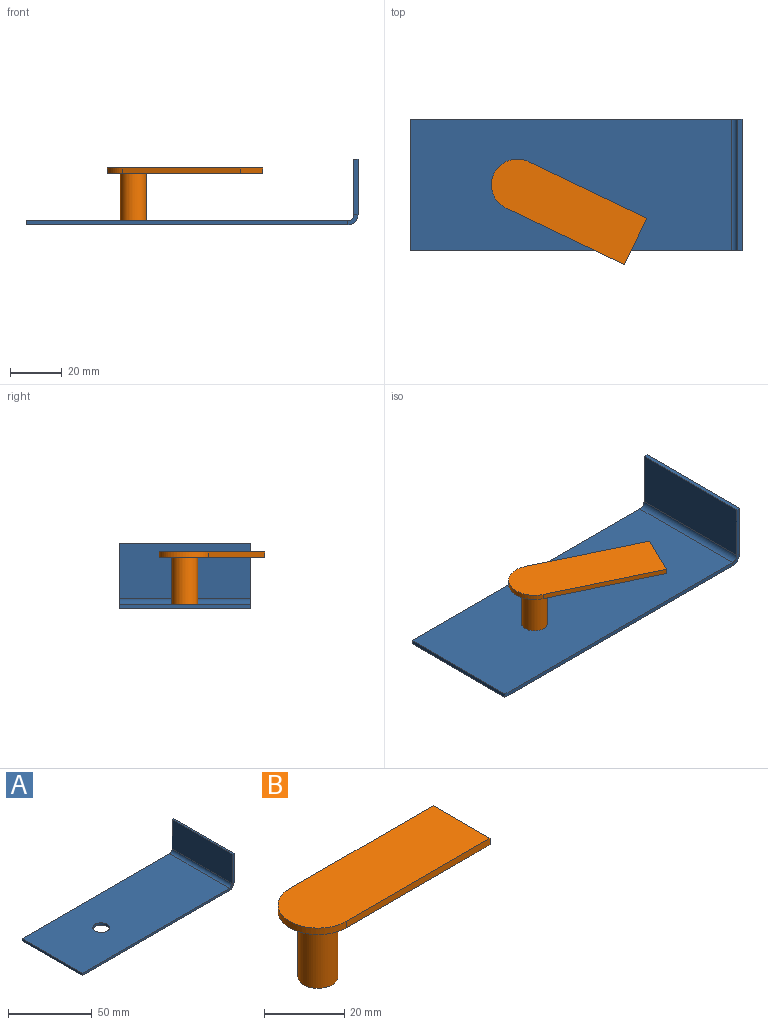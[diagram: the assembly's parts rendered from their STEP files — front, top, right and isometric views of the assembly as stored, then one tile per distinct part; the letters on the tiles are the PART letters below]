
ASSEMBLY  parts=2 mates=1
PART A: 15 faces, bbox 128.6x50.8x25.4 mm
  f0: plane 50.8x1.59mm, normal (-1,0,0), area 80.6mm2, adj f1,f2,f3,f4
  f1: plane 124.71x1.59mm, normal (0,1,0), area 198mm2, adj f0,f3,f4,f11
  f2: plane 124.71x1.59mm, normal (0,-1,0), area 198mm2, adj f0,f3,f4,f10
  f3: plane 124.71x50.8mm, normal (0,0,-1), area 6256.9mm2, adj f0,f1,f2,f12,f14
  f4: plane 124.71x50.8mm, normal (0,0,1), area 6256.9mm2, adj f0,f1,f2,f13,f14
  f5: plane 50.8x1.59mm, normal (0,0,1), area 80.6mm2, adj f6,f7,f8,f9
  f6: plane 21.53x1.59mm, normal (0,-1,0), area 34.2mm2, adj f5,f8,f9,f10
  f7: plane 21.53x1.59mm, normal (0,1,0), area 34.2mm2, adj f5,f8,f9,f11
  f8: plane 50.8x21.53mm, normal (1,0,0), area 1093.5mm2, adj f5,f6,f7,f12
  f9: plane 50.8x21.53mm, normal (-1,0,0), area 1093.5mm2, adj f5,f6,f7,f13
  f10: plane 3.87x3.87mm, normal (0,-1,0), area 7.7mm2, adj f2,f6,f12,f13
  f11: plane 3.87x3.87mm, normal (0,1,0), area 7.7mm2, adj f1,f7,f12,f13
  f12: cylinder r=3.87mm len=50.8mm, axis (0,-1,0), area 309.1mm2, adj f3,f8,f10,f11
  f13: cylinder r=2.29mm len=50.8mm, axis (0,-1,0), area 182.4mm2, adj f4,f9,f10,f11
  f14: cylinder r=5mm len=10mm, axis (0,0,1), area 49.9mm2, adj f3,f4
PART B: 8 faces, bbox 60.8x20x22 mm
  f0: cylinder r=5mm len=20mm, axis (0,0,1), area 628.3mm2, adj f1,f7
  f1: plane 10x10mm, normal (0,0,-1), area 78.5mm2, adj f0
  f2: plane 50.8x2mm, normal (0,1,0), area 101.6mm2, adj f3,f5,f6,f7
  f3: cylinder r=10mm len=20mm, axis (0,0,-1), area 62.8mm2, adj f2,f4,f6,f7
  f4: plane 50.8x2mm, normal (0,-1,0), area 101.6mm2, adj f3,f5,f6,f7
  f5: plane 20x2mm, normal (1,0,0), area 40mm2, adj f2,f4,f6,f7
  f6: plane 60.8x20mm, normal (0,0,1), area 1173.1mm2, adj f2,f3,f4,f5
  f7: plane 60.8x20mm, normal (0,0,-1), area 1094.5mm2, adj f0,f2,f3,f4,f5
PLACE A t=(-10.48,-1.53,-6.62)mm fixed
PLACE B rot(axis=(0,0,-1),25.6deg) t=(-12.62,-11,11.8)mm
MATE revolute B.f0 <-> A.f14  axis (0,0,-1) through (-32.43,-1.53,-6.62)mm
